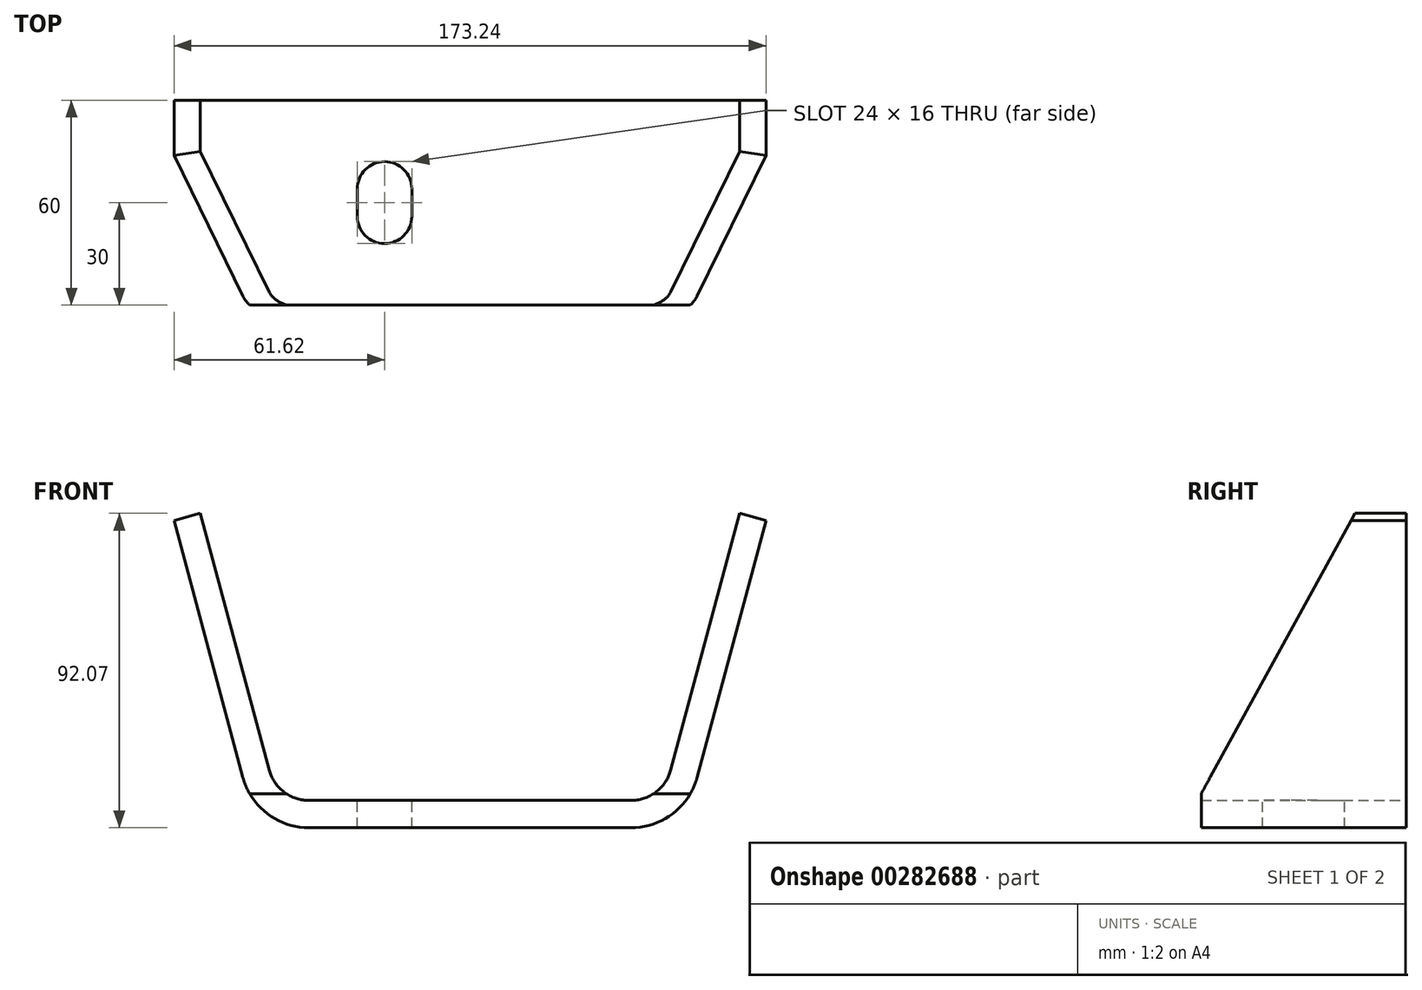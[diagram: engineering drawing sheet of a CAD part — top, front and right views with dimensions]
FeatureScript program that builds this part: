
annotation { "Feature Type Name" : "Feature", "Feature Type Description" : "" }
export const myFeature = defineFeature(function(context is Context, id is Id, definition is map)
    precondition{}
    {
        {
            var Q0;
            Q0=qCreatedBy(makeId("Front.planeOp"),FACE);
            var sketch = newSketch(context, id + "F0", { "sketchPlane" : qUnion([Q0])});
            skLineSegment(sketch, "E0", {"start": v(-47.15, 0) * mm, "end": v(47.15, 0) * mm});
            skLineSegment(sketch, "E1", {"start": v(66.47, 14.82) * mm, "end": v(86.62, 90) * mm});
            skLineSegment(sketch, "E2", {"start": v(0, 0) * mm, "end": v(0, 112.33) * mm, "construction": true});
            skLineSegment(sketch, "E3.MirrorCS", {"start": v(-66.47, 14.82) * mm, "end": v(-86.62, 90) * mm});
            skLineSegment(sketch, "E4.0", {"start": v(-58.74, 16.9) * mm, "end": v(-78.89, 92.07) * mm});
            skLineSegment(sketch, "E4.1", {"start": v(-47.15, 8) * mm, "end": v(47.15, 8) * mm});
            skLineSegment(sketch, "E4.2", {"start": v(58.74, 16.9) * mm, "end": v(78.89, 92.07) * mm});
            skLineSegment(sketch, "E5", {"start": v(-86.62, 90) * mm, "end": v(-78.89, 92.07) * mm});
            skLineSegment(sketch, "E6", {"start": v(78.89, 92.07) * mm, "end": v(86.62, 90) * mm});
            skPoint(sketch, "E7.visualSharp", {"position": v(-56.36, 8) * mm});
            skArc(sketch, "E7.filletArc", {"start": v(-58.74, 16.9) * mm, "mid": v(-54.46, 10.48) * mm, "end": v(-47.15, 8) * mm});
            skPoint(sketch, "E8.visualSharp", {"position": v(56.36, 8) * mm});
            skArc(sketch, "E8.filletArc", {"start": v(47.15, 8) * mm, "mid": v(54.46, 10.48) * mm, "end": v(58.74, 16.9) * mm});
            skPoint(sketch, "E9.visualSharp", {"position": v(-62.5, 0) * mm});
            skArc(sketch, "E9.filletArc", {"start": v(-66.47, 14.82) * mm, "mid": v(-59.33, 4.13) * mm, "end": v(-47.15, 0) * mm});
            skPoint(sketch, "E10.visualSharp", {"position": v(62.5, 0) * mm});
            skArc(sketch, "E10.filletArc", {"start": v(47.15, 0) * mm, "mid": v(59.33, 4.13) * mm, "end": v(66.47, 14.82) * mm});
            skSolve(sketch);
        }
        {
            var Q0;
            Q0=makeQuery(id+"F0.imprint","IMPRINT",FACE,{"disambiguationData":[TD([[makeQuery(id+"F0.imprint","IMPRINT",EDGE,{"derivedFrom":sQuery(id+"F0.wireOp",EDGE,"E0")}),1.0]])]});
            extrude(context, id + "F1", {"entities" : qUnion([Q0]), "depth" : 60 * mm});
        }
        {
            var Q0;
            Q0=qCreatedBy(makeId("Right.planeOp"),FACE);
            var sketch = newSketch(context, id + "F2", { "sketchPlane" : qUnion([Q0])});
            skLineSegment(sketch, "E11.0", {"start": v(-60, 92.07) * mm, "end": v(-15, 92.07) * mm});
            skLineSegment(sketch, "E12", {"start": v(-15, 92.07) * mm, "end": v(-60, 10) * mm});
            skLineSegment(sketch, "E13", {"start": v(-60, 92.07) * mm, "end": v(-60, 10) * mm});
            skPoint(sketch, "E14.orphan", {"position": v(0, 92.07) * mm});
            skSolve(sketch);
        }
        {
            var Q0;
            Q0=makeQuery(id+"F2.imprint","IMPRINT",FACE,{"disambiguationData":[TD([[makeQuery(id+"F2.imprint","IMPRINT",EDGE,{"derivedFrom":sQuery(id+"F2.wireOp",EDGE,"E11.0")}),-1.0]])]});
            extrude(context, id + "F3", {"entities" : qUnion([Q0]), "operationType" : NewBodyOperationType.REMOVE, "endBound" : BoundingType.THROUGH_ALL, "oppositeDirection" : true, "depth" : 25 * mm, "hasSecondDirection" : true, "secondDirectionBound" : BoundingType.THROUGH_ALL, "secondDirectionOppositeDirection" : false, "secondDirectionDepth" : 25 * mm});
        }
        {
            var Q0;
            Q0=makeQuery(id+"F1.opExtrude","SWEPT_FACE",FACE,{"disambiguationData":[OSD([sQuery(id+"F0.wireOp",EDGE,"E4.1")])]});
            var sketch = newSketch(context, id + "F4", { "sketchPlane" : qUnion([Q0])});
            skLineSegment(sketch, "E15", {"start": v(-42.86, -34) * mm, "end": v(48.61, -34) * mm, "construction": true});
            skLineSegment(sketch, "E16", {"start": v(-25, -42) * mm, "end": v(-25, -18) * mm, "construction": true});
            skArc(sketch, "E17", {"start": v(-33, -34) * mm, "mid": v(-25, -42) * mm, "end": v(-17, -34) * mm});
            skArc(sketch, "E18", {"start": v(-17, -26) * mm, "mid": v(-25, -18) * mm, "end": v(-33, -26) * mm});
            skLineSegment(sketch, "E19", {"start": v(-33, -26) * mm, "end": v(-33, -34) * mm});
            skLineSegment(sketch, "E20", {"start": v(-17, -26) * mm, "end": v(-17, -34) * mm});
            skPoint(sketch, "E21.orphan", {"position": v(-25, 27.84) * mm});
            skArc(sketch, "E22.MirrorCS", {"start": v(17, -26) * mm, "mid": v(25, -18) * mm, "end": v(33, -26) * mm});
            skLineSegment(sketch, "E23.MirrorCS", {"start": v(25, -42) * mm, "end": v(25, -18) * mm, "construction": true});
            skLineSegment(sketch, "E24.MirrorCS", {"start": v(33, -26) * mm, "end": v(33, -34) * mm});
            skArc(sketch, "E25.MirrorCS", {"start": v(33, -34) * mm, "mid": v(25, -42) * mm, "end": v(17, -34) * mm});
            skLineSegment(sketch, "E26.MirrorCS", {"start": v(17, -26) * mm, "end": v(17, -34) * mm});
            skSolve(sketch);
        }
        {
            var Q0;
            Q0=makeQuery(id+"F4.imprint","IMPRINT",FACE,{"disambiguationData":[TD([[makeQuery(id+"F4.imprint","IMPRINT",EDGE,{"derivedFrom":sQuery(id+"F4.wireOp",EDGE,"E17")}),1.0]])]});
            var Q1;
            Q1=makeQuery(id+"F4.imprint","IMPRINT",FACE,{"disambiguationData":[TD([[makeQuery(id+"F4.imprint","IMPRINT",EDGE,{"derivedFrom":sQuery(id+"F4.wireOp",EDGE,"E22.MirrorCS")}),-1.0]])]});
            extrude(context, id + "F5", {"entities" : qUnion([Q0, Q1]), "operationType" : NewBodyOperationType.REMOVE, "endBound" : BoundingType.THROUGH_ALL, "oppositeDirection" : true, "depth" : 25 * mm});
        }
    });
